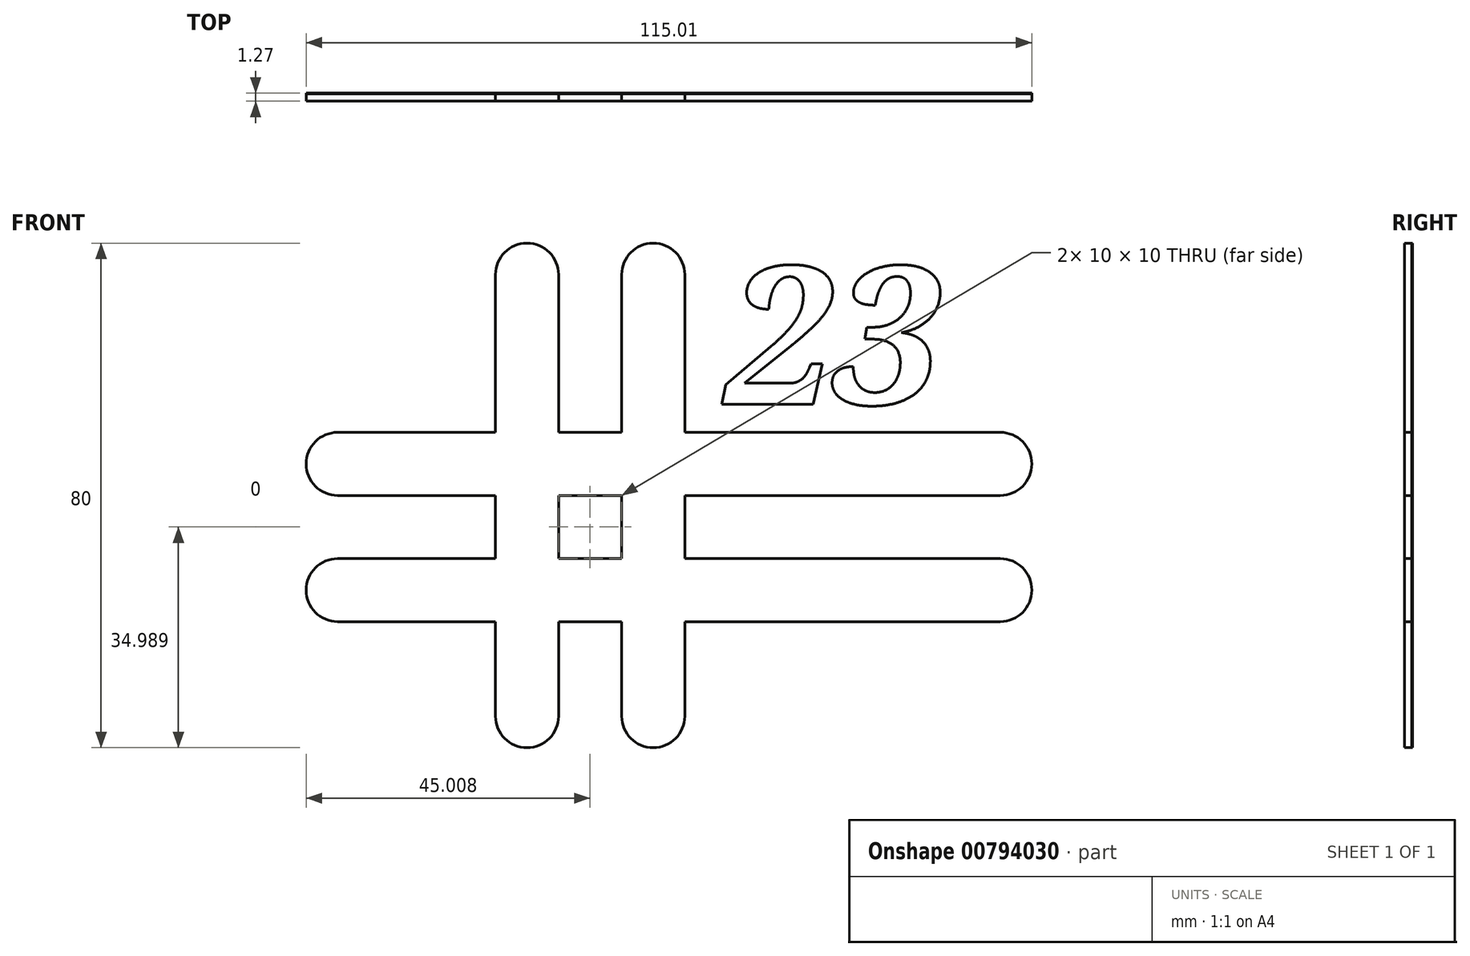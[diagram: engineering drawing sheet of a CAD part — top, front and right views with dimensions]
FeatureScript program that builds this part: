
annotation { "Feature Type Name" : "Feature", "Feature Type Description" : "" }
export const myFeature = defineFeature(function(context is Context, id is Id, definition is map)
    precondition{}
    {
        {
            var Q0;
            Q0=qCreatedBy(makeId("Front.planeOp"),FACE);
            var sketch = newSketch(context, id + "F0", { "sketchPlane" : qUnion([Q0])});
            skLineSegment(sketch, "E0", {"start": v(-54.6, 14.47) * mm, "end": v(-54.6, 29.45) * mm});
            skLineSegment(sketch, "E1", {"start": v(-44.6, 84.47) * mm, "end": v(-44.6, 59.47) * mm});
            skArc(sketch, "E2", {"start": v(-44.6, 84.47) * mm, "mid": v(-49.6, 89.47) * mm, "end": v(-54.6, 84.47) * mm});
            skArc(sketch, "E3", {"start": v(-54.6, 14.47) * mm, "mid": v(-49.6, 9.47) * mm, "end": v(-44.6, 14.47) * mm});
            skLineSegment(sketch, "E4", {"start": v(-34.6, 84.47) * mm, "end": v(-34.6, 59.47) * mm});
            skArc(sketch, "E5", {"start": v(-24.6, 84.47) * mm, "mid": v(-29.6, 89.47) * mm, "end": v(-34.6, 84.47) * mm});
            skLineSegment(sketch, "E6", {"start": v(-24.6, 84.47) * mm, "end": v(-24.6, 59.47) * mm});
            skArc(sketch, "E7", {"start": v(-34.6, 14.47) * mm, "mid": v(-29.6, 9.47) * mm, "end": v(-24.6, 14.47) * mm});
            skLineSegment(sketch, "E8", {"start": v(-79.6, 59.47) * mm, "end": v(-54.6, 59.47) * mm});
            skLineSegment(sketch, "E9", {"start": v(-79.6, 49.46) * mm, "end": v(-54.6, 49.46) * mm});
            skArc(sketch, "E10", {"start": v(-79.6, 59.47) * mm, "mid": v(-84.6, 54.46) * mm, "end": v(-79.6, 49.46) * mm});
            skArc(sketch, "E11", {"start": v(25.4, 49.46) * mm, "mid": v(30.41, 54.46) * mm, "end": v(25.4, 59.47) * mm});
            skPoint(sketch, "E12", {"position": v(-54.6, 59.47) * mm});
            skPoint(sketch, "E13", {"position": v(-54.6, 39.46) * mm});
            skLineSegment(sketch, "E14", {"start": v(-79.6, 39.46) * mm, "end": v(-54.6, 39.46) * mm});
            skLineSegment(sketch, "E15", {"start": v(-79.6, 29.45) * mm, "end": v(-54.6, 29.45) * mm});
            skArc(sketch, "E16", {"start": v(-79.6, 39.46) * mm, "mid": v(-84.6, 34.46) * mm, "end": v(-79.6, 29.45) * mm});
            skArc(sketch, "E17", {"start": v(25.4, 29.45) * mm, "mid": v(30.41, 34.46) * mm, "end": v(25.4, 39.46) * mm});
            skPoint(sketch, "E18", {"position": v(-54.6, 49.46) * mm});
            skPoint(sketch, "E19", {"position": v(-44.6, 59.47) * mm});
            skPoint(sketch, "E20", {"position": v(-44.6, 49.46) * mm});
            skLineSegment(sketch, "E21.trimOffspring", {"start": v(-44.6, 59.47) * mm, "end": v(-34.6, 59.47) * mm});
            skLineSegment(sketch, "E22.trimOffspring", {"start": v(-54.6, 59.47) * mm, "end": v(-54.6, 84.47) * mm});
            skLineSegment(sketch, "E23.trimOffspring", {"start": v(-44.6, 49.46) * mm, "end": v(-44.6, 39.46) * mm});
            skLineSegment(sketch, "E24.trimOffspring", {"start": v(-44.6, 49.46) * mm, "end": v(-34.6, 49.46) * mm});
            skPoint(sketch, "E25", {"position": v(-34.6, 59.47) * mm});
            skPoint(sketch, "E26", {"position": v(-24.6, 59.47) * mm});
            skPoint(sketch, "E27", {"position": v(-24.6, 49.46) * mm});
            skPoint(sketch, "E28", {"position": v(-34.6, 49.46) * mm});
            skPoint(sketch, "E29", {"position": v(-34.6, 39.46) * mm});
            skPoint(sketch, "E30", {"position": v(-24.6, 39.46) * mm});
            skPoint(sketch, "E31", {"position": v(-24.6, 29.45) * mm});
            skPoint(sketch, "E32", {"position": v(-34.6, 29.45) * mm});
            skPoint(sketch, "E33", {"position": v(-44.6, 39.46) * mm});
            skPoint(sketch, "E34", {"position": v(-44.6, 29.45) * mm});
            skPoint(sketch, "E35", {"position": v(-54.6, 29.45) * mm});
            skLineSegment(sketch, "E36.trimOffspring", {"start": v(-44.6, 39.46) * mm, "end": v(-34.6, 39.46) * mm});
            skLineSegment(sketch, "E37.trimOffspring", {"start": v(-54.6, 39.46) * mm, "end": v(-54.6, 49.46) * mm});
            skLineSegment(sketch, "E38.trimOffspring", {"start": v(-44.6, 29.45) * mm, "end": v(-44.6, 14.47) * mm});
            skLineSegment(sketch, "E39.trimOffspring", {"start": v(-44.6, 29.45) * mm, "end": v(-34.6, 29.45) * mm});
            skLineSegment(sketch, "E40.trimOffspring", {"start": v(-34.6, 29.45) * mm, "end": v(-34.6, 14.47) * mm});
            skLineSegment(sketch, "E41.trimOffspring", {"start": v(-24.6, 29.45) * mm, "end": v(-24.6, 14.47) * mm});
            skLineSegment(sketch, "E42.trimOffspring", {"start": v(-24.6, 29.45) * mm, "end": v(25.4, 29.45) * mm});
            skLineSegment(sketch, "E43.trimOffspring", {"start": v(-24.6, 39.46) * mm, "end": v(25.4, 39.46) * mm});
            skLineSegment(sketch, "E44.trimOffspring", {"start": v(-24.6, 49.46) * mm, "end": v(25.4, 49.46) * mm});
            skLineSegment(sketch, "E45.trimOffspring", {"start": v(-34.6, 49.46) * mm, "end": v(-34.6, 39.46) * mm});
            skLineSegment(sketch, "E46.trimOffspring", {"start": v(-24.6, 49.46) * mm, "end": v(-24.6, 39.46) * mm});
            skLineSegment(sketch, "E47.trimOffspring", {"start": v(-24.6, 59.47) * mm, "end": v(25.4, 59.47) * mm});
            skText(sketch, "E48", { "text": "23", "fontName": "NotoSerif-BoldItalic.ttf"});
            const initialGuessF0  = {"E48": [-0.0183, 0.06391, 1, 0, 0.022]};
            skSetInitialGuess(sketch, initialGuessF0);
            skSolve(sketch);
        }
        {
            var Q0;
            Q0=makeQuery(id+"F0.imprint","IMPRINT",FACE,{"disambiguationData":[TD([[makeQuery(id+"F0.imprint","IMPRINT",EDGE,{"derivedFrom":sQuery(id+"F0.wireOp",EDGE,"E0")}),-1.0]])]});
            var Q1;
            Q1=makeQuery(id+"F0.imprint","IMPRINT",FACE,{"disambiguationData":[TD([[makeQuery(id+"F0.imprint","IMPRINT",EDGE,{"derivedFrom":sQuery(id+"F0.wireOp",EDGE,"E4")}),1.0]])]});
            extrude(context, id + "F1", {"entities" : qUnion([Q0, Q1]), "depth" : 1.27 * mm, "offsetDistance" : 25.4 * mm});
        }
        {
            var Q0;
            Q0 = qSketchRegion(id + "F0", true);
            extrude(context, id + "F2", {"entities" : qUnion([Q0]), "depth" : 0.1 * mm, "offsetDistance" : 25.4 * mm});
        }
    });
